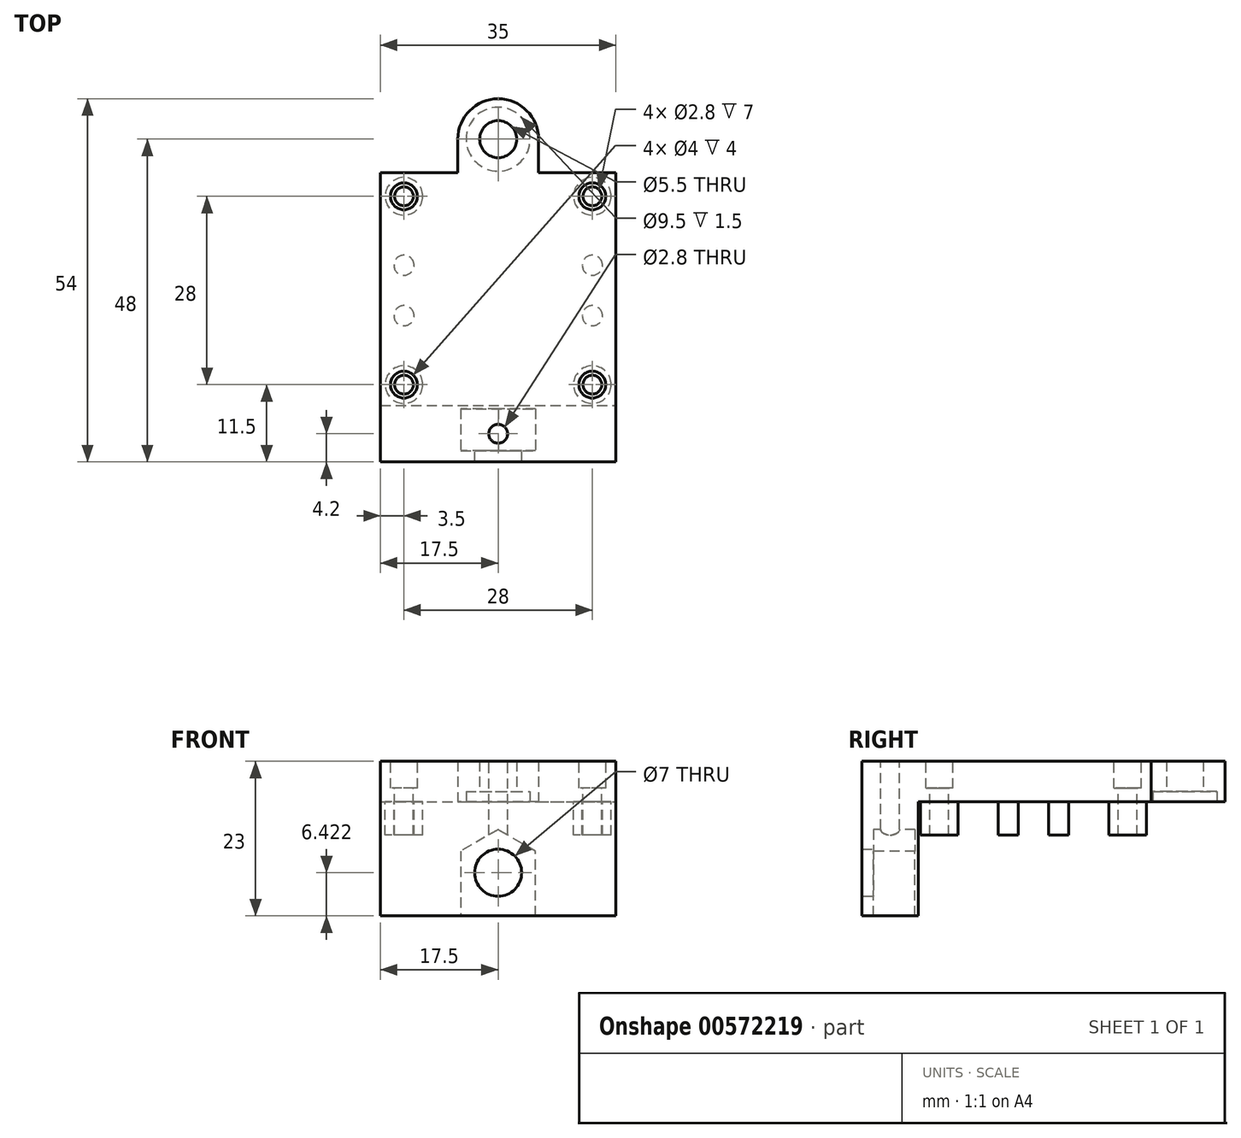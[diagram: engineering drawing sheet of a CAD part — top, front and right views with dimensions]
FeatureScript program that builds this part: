
annotation { "Feature Type Name" : "Feature", "Feature Type Description" : "" }
export const myFeature = defineFeature(function(context is Context, id is Id, definition is map)
    precondition{}
    {
        {
            var Q0;
            Q0=qCreatedBy(makeId("Top.planeOp"),FACE);
            var sketch = newSketch(context, id + "F0", { "sketchPlane" : qUnion([Q0])});
            skLineSegment(sketch, "E0.bottom", {"start": v(-14, 14) * mm, "end": v(14, 14) * mm, "construction": true});
            skLineSegment(sketch, "E0.top", {"start": v(-14, -14) * mm, "end": v(14, -14) * mm, "construction": true});
            skLineSegment(sketch, "E0.left", {"start": v(-14, 14) * mm, "end": v(-14, -14) * mm, "construction": true});
            skLineSegment(sketch, "E0.right", {"start": v(14, 14) * mm, "end": v(14, -14) * mm, "construction": true});
            skPoint(sketch, "E0.middle", {"position": v(0, 0) * mm});
            skLineSegment(sketch, "E1.bottom", {"start": v(-17.5, 17.5) * mm, "end": v(17.5, 17.5) * mm});
            skLineSegment(sketch, "E1.top", {"start": v(-17.5, -17.5) * mm, "end": v(17.5, -17.5) * mm});
            skLineSegment(sketch, "E1.left", {"start": v(-17.5, 17.5) * mm, "end": v(-17.5, -17.5) * mm});
            skLineSegment(sketch, "E1.right", {"start": v(17.5, 17.5) * mm, "end": v(17.5, -17.5) * mm});
            skLineSegment(sketch, "E2.bottom", {"start": v(-6, 22.5) * mm, "end": v(6, 22.5) * mm});
            skPoint(sketch, "E2.middle", {"position": v(0, 17.5) * mm});
            skCircle(sketch, "E3", {"center": v(0, 22.5) * mm, "radius": 6 * mm});
            skLineSegment(sketch, "E4.top", {"start": v(-6, 17.5) * mm, "end": v(6, 17.5) * mm});
            skLineSegment(sketch, "E4.left", {"start": v(-6, 22.5) * mm, "end": v(-6, 17.5) * mm});
            skLineSegment(sketch, "E4.right", {"start": v(6, 22.5) * mm, "end": v(6, 17.5) * mm});
            skCircle(sketch, "E5", {"center": v(-14, 14) * mm, "radius": 2.8 * mm});
            skCircle(sketch, "E6", {"center": v(-14, -14) * mm, "radius": 2.8 * mm});
            skCircle(sketch, "E7", {"center": v(14, -14) * mm, "radius": 2.8 * mm});
            skCircle(sketch, "E8", {"center": v(14, 14) * mm, "radius": 2.8 * mm});
            skCircle(sketch, "E9", {"center": v(-14, 3.75) * mm, "radius": 1.5 * mm});
            skCircle(sketch, "E10", {"center": v(-14, -3.75) * mm, "radius": 1.5 * mm});
            skLineSegment(sketch, "E11", {"start": v(-14, 2.25) * mm, "end": v(-14, -2.25) * mm, "construction": true});
            skPoint(sketch, "E12", {"position": v(-14, 0) * mm});
            skPoint(sketch, "E13", {"position": v(-14, 2.25) * mm});
            skPoint(sketch, "E14", {"position": v(-14, -2.25) * mm});
            skCircle(sketch, "E15", {"center": v(14, -3.75) * mm, "radius": 1.5 * mm});
            skCircle(sketch, "E16", {"center": v(14, 3.75) * mm, "radius": 1.5 * mm});
            skSolve(sketch);
        }
        {
            var Q0;
            Q0=makeQuery(id+"F0.imprint","IMPRINT",FACE,{"disambiguationData":[TD([[makeQuery(id+"F0.imprint","IMPRINT",EDGE,{"derivedFrom":sQuery(id+"F0.wireOp",EDGE,"E1.top")}),1.0]])]});
            var Q1;
            {var subQ0=sQuery(id+"F0.wireOp",EDGE,"E2.bottom");Q1=makeQuery(id+"F0.imprint","IMPRINT",FACE,{"disambiguationData":[TD([[makeQuery(id+"F0.imprint","IMPRINT",EDGE,{"derivedFrom":subQ0}),-1.0]])]});}
            var Q2;
            {var subQ0=sQuery(id+"F0.wireOp",EDGE,"E2.bottom");Q2=makeQuery(id+"F0.imprint","IMPRINT",FACE,{"disambiguationData":[TD([[makeQuery(id+"F0.imprint","IMPRINT",EDGE,{"derivedFrom":subQ0}),1.0]])]});}
            var Q3;
            {var subQ0=sQuery(id+"F0.wireOp",EDGE,"E4.right");Q3=makeQuery(id+"F0.imprint","IMPRINT",FACE,{"disambiguationData":[TD([[makeQuery(id+"F0.imprint","IMPRINT",EDGE,{"derivedFrom":subQ0}),-1.0]])]});}
            var Q4;
            {var subQ0=sQuery(id+"F0.wireOp",EDGE,"E4.top");var subQ1=sQuery(id+"F0.wireOp",EDGE,"E3");var subQ2=makeQuery(id+"F0.imprint","INTERSECT",VERTEX,{"disambiguationData":[OD(0.0)],"derivedFrom":[subQ1,subQ0]});Q4=makeQuery(id+"F0.imprint","IMPRINT",FACE,{"disambiguationData":[TD([[makeQuery(id+"F0.imprint","IMPRINT",EDGE,{"disambiguationData":[TD([[subQ2,-1.0]])],"derivedFrom":subQ1}),1.0]])]});}
            var Q5;
            {var subQ0=sQuery(id+"F0.wireOp",EDGE,"E4.left");Q5=makeQuery(id+"F0.imprint","IMPRINT",FACE,{"disambiguationData":[TD([[makeQuery(id+"F0.imprint","IMPRINT",EDGE,{"derivedFrom":subQ0}),1.0]])]});}
            var Q6;
            Q6=makeQuery(id+"F0.imprint","IMPRINT",FACE,{"disambiguationData":[TD([[makeQuery(id+"F0.imprint","IMPRINT",EDGE,{"derivedFrom":sQuery(id+"F0.wireOp",EDGE,"E6")}),1.0]])]});
            var Q7;
            Q7=makeQuery(id+"F0.imprint","IMPRINT",FACE,{"disambiguationData":[TD([[makeQuery(id+"F0.imprint","IMPRINT",EDGE,{"derivedFrom":sQuery(id+"F0.wireOp",EDGE,"E7")}),1.0]])]});
            var Q8;
            Q8=makeQuery(id+"F0.imprint","IMPRINT",FACE,{"disambiguationData":[TD([[makeQuery(id+"F0.imprint","IMPRINT",EDGE,{"derivedFrom":sQuery(id+"F0.wireOp",EDGE,"E8")}),1.0]])]});
            var Q9;
            Q9=makeQuery(id+"F0.imprint","IMPRINT",FACE,{"disambiguationData":[TD([[makeQuery(id+"F0.imprint","IMPRINT",EDGE,{"derivedFrom":sQuery(id+"F0.wireOp",EDGE,"E5")}),1.0]])]});
            var Q10;
            Q10=makeQuery(id+"F0.imprint","IMPRINT",FACE,{"disambiguationData":[TD([[makeQuery(id+"F0.imprint","IMPRINT",EDGE,{"derivedFrom":sQuery(id+"F0.wireOp",EDGE,"E9")}),1.0]])]});
            var Q11;
            Q11=makeQuery(id+"F0.imprint","IMPRINT",FACE,{"disambiguationData":[TD([[makeQuery(id+"F0.imprint","IMPRINT",EDGE,{"derivedFrom":sQuery(id+"F0.wireOp",EDGE,"E10")}),1.0]])]});
            var Q12;
            Q12=makeQuery(id+"F0.imprint","IMPRINT",FACE,{"disambiguationData":[TD([[makeQuery(id+"F0.imprint","IMPRINT",EDGE,{"derivedFrom":sQuery(id+"F0.wireOp",EDGE,"E15")}),1.0]])]});
            var Q13;
            Q13=makeQuery(id+"F0.imprint","IMPRINT",FACE,{"disambiguationData":[TD([[makeQuery(id+"F0.imprint","IMPRINT",EDGE,{"derivedFrom":sQuery(id+"F0.wireOp",EDGE,"E16")}),1.0]])]});
            extrude(context, id + "F1", {"entities" : qUnion([Q0, Q1, Q2, Q3, Q4, Q5, Q6, Q7, Q8, Q9, Q10, Q11, Q12, Q13]), "depth" : 6 * mm, "offsetDistance" : 25 * mm});
        }
        {
            var Q0;
            Q0=makeQuery(id+"F0.imprint","IMPRINT",FACE,{"disambiguationData":[TD([[makeQuery(id+"F0.imprint","IMPRINT",EDGE,{"derivedFrom":sQuery(id+"F0.wireOp",EDGE,"E6")}),1.0]])]});
            var Q1;
            Q1=makeQuery(id+"F0.imprint","IMPRINT",FACE,{"disambiguationData":[TD([[makeQuery(id+"F0.imprint","IMPRINT",EDGE,{"derivedFrom":sQuery(id+"F0.wireOp",EDGE,"E5")}),1.0]])]});
            var Q2;
            Q2=makeQuery(id+"F0.imprint","IMPRINT",FACE,{"disambiguationData":[TD([[makeQuery(id+"F0.imprint","IMPRINT",EDGE,{"derivedFrom":sQuery(id+"F0.wireOp",EDGE,"E8")}),1.0]])]});
            var Q3;
            Q3=makeQuery(id+"F0.imprint","IMPRINT",FACE,{"disambiguationData":[TD([[makeQuery(id+"F0.imprint","IMPRINT",EDGE,{"derivedFrom":sQuery(id+"F0.wireOp",EDGE,"E7")}),1.0]])]});
            var Q4;
            Q4=makeQuery(id+"F0.imprint","IMPRINT",FACE,{"disambiguationData":[TD([[makeQuery(id+"F0.imprint","IMPRINT",EDGE,{"derivedFrom":sQuery(id+"F0.wireOp",EDGE,"E9")}),1.0]])]});
            var Q5;
            Q5=makeQuery(id+"F0.imprint","IMPRINT",FACE,{"disambiguationData":[TD([[makeQuery(id+"F0.imprint","IMPRINT",EDGE,{"derivedFrom":sQuery(id+"F0.wireOp",EDGE,"E10")}),1.0]])]});
            var Q6;
            Q6=makeQuery(id+"F0.imprint","IMPRINT",FACE,{"disambiguationData":[TD([[makeQuery(id+"F0.imprint","IMPRINT",EDGE,{"derivedFrom":sQuery(id+"F0.wireOp",EDGE,"E15")}),1.0]])]});
            var Q7;
            Q7=makeQuery(id+"F0.imprint","IMPRINT",FACE,{"disambiguationData":[TD([[makeQuery(id+"F0.imprint","IMPRINT",EDGE,{"derivedFrom":sQuery(id+"F0.wireOp",EDGE,"E16")}),1.0]])]});
            extrude(context, id + "F2", {"entities" : qUnion([Q0, Q1, Q2, Q3, Q4, Q5, Q6, Q7]), "operationType" : NewBodyOperationType.ADD, "oppositeDirection" : true, "depth" : 5 * mm, "offsetDistance" : 25 * mm});
        }
        {
            var Q0;
            Q0=sQuery(id+"F0.wireOp",VERTEX,"E3.center");
            var Q1;
            Q1=makeQuery(id+"F1.opExtrude","SWEPT_BODY",BODY,{"disambiguationData":[OSD([sQuery(id+"F0.wireOp",EDGE,"E1.bottom"),sQuery(id+"F0.wireOp",EDGE,"E1.top"),sQuery(id+"F0.wireOp",EDGE,"E1.left"),sQuery(id+"F0.wireOp",EDGE,"E1.right"),sQuery(id+"F0.wireOp",EDGE,"E3"),sQuery(id+"F0.wireOp",EDGE,"E4.left"),sQuery(id+"F0.wireOp",EDGE,"E4.right")])]});
            hole(context, id + "F3", {"style" : HoleStyle.C_BORE, "endStyle" : HoleEndStyle.BLIND, "oppositeDirection" : true, "holeDiameter" : 5.5 * mm, "cBoreDiameter" : 9.5 * mm, "cBoreDepth" : 1.5 * mm, "majorDiameter" : 5 * mm, "holeDepth" : 30 * mm, "isTappedThrough" : true, "tappedDepth" : 10.5 * mm, "tapClearance" : 3, "locations" : qUnion([Q0]), "scope" : qUnion([Q1])});
        }
        {
            var Q0;
            Q0=makeQuery(id+"F1.opExtrude","CAP_FACE",FACE,{"disambiguationData":[OSD([sQuery(id+"F0.wireOp",EDGE,"E1.bottom"),sQuery(id+"F0.wireOp",EDGE,"E1.top"),sQuery(id+"F0.wireOp",EDGE,"E1.left"),sQuery(id+"F0.wireOp",EDGE,"E1.right"),sQuery(id+"F0.wireOp",EDGE,"E3"),sQuery(id+"F0.wireOp",EDGE,"E4.left"),sQuery(id+"F0.wireOp",EDGE,"E4.right")])],"isStart":false});
            var sketch = newSketch(context, id + "F4", { "sketchPlane" : qUnion([Q0])});
            skPoint(sketch, "E17", {"position": v(-14, 14) * mm});
            skPoint(sketch, "E18", {"position": v(14, 14) * mm});
            skPoint(sketch, "E19", {"position": v(-14, -14) * mm});
            skPoint(sketch, "E20", {"position": v(14, -14) * mm});
            skSolve(sketch);
        }
        {
            var Q0;
            Q0=sQuery(id+"F4.wireOp",VERTEX,"E17");
            var Q1;
            Q1=sQuery(id+"F4.wireOp",VERTEX,"E18");
            var Q2;
            Q2=sQuery(id+"F4.wireOp",VERTEX,"E20");
            var Q3;
            Q3=sQuery(id+"F4.wireOp",VERTEX,"E19");
            var Q4;
            Q4=makeQuery(id+"F1.opExtrude","SWEPT_BODY",BODY,{"disambiguationData":[OSD([sQuery(id+"F0.wireOp",EDGE,"E1.bottom"),sQuery(id+"F0.wireOp",EDGE,"E1.top"),sQuery(id+"F0.wireOp",EDGE,"E1.left"),sQuery(id+"F0.wireOp",EDGE,"E1.right"),sQuery(id+"F0.wireOp",EDGE,"E3"),sQuery(id+"F0.wireOp",EDGE,"E4.left"),sQuery(id+"F0.wireOp",EDGE,"E4.right")])]});
            hole(context, id + "F5", {"style" : HoleStyle.C_BORE, "endStyle" : HoleEndStyle.THROUGH, "holeDiameter" : 2.8 * mm, "cBoreDiameter" : 4 * mm, "cBoreDepth" : 4 * mm, "majorDiameter" : 5 * mm, "isTappedThrough" : true, "tappedDepth" : 10.5 * mm, "tapClearance" : 3, "locations" : qUnion([Q0, Q1, Q2, Q3]), "scope" : qUnion([Q4])});
        }
        {
            var Q0;
            Q0=makeQuery(id+"F1.opExtrude","SWEPT_FACE",FACE,{"disambiguationData":[OSD([sQuery(id+"F0.wireOp",EDGE,"E1.top")])]});
            var sketch = newSketch(context, id + "F6", { "sketchPlane" : qUnion([Q0])});
            skLineSegment(sketch, "E21.bottom", {"start": v(-17.5, 6) * mm, "end": v(17.5, 6) * mm});
            skLineSegment(sketch, "E21.top", {"start": v(-17.5, -17) * mm, "end": v(17.5, -17) * mm});
            skLineSegment(sketch, "E21.left", {"start": v(-17.5, 6) * mm, "end": v(-17.5, -17) * mm});
            skLineSegment(sketch, "E21.right", {"start": v(17.5, 6) * mm, "end": v(17.5, -17) * mm});
            skSolve(sketch);
        }
        {
            var Q0;
            {var subQ0=sQuery(id+"F6.wireOp",EDGE,"E21.top");Q0=makeQuery(id+"F6.imprint","IMPRINT",FACE,{"disambiguationData":[TD([[makeQuery(id+"F6.imprint","IMPRINT",EDGE,{"derivedFrom":subQ0}),1.0]])]});}
            var Q1;
            {var subQ0=sQuery(id+"F6.wireOp",EDGE,"E21.bottom");Q1=makeQuery(id+"F6.imprint","IMPRINT",FACE,{"disambiguationData":[TD([[makeQuery(id+"F6.imprint","IMPRINT",EDGE,{"derivedFrom":subQ0}),-1.0]])]});}
            extrude(context, id + "F7", {"entities" : qUnion([Q0, Q1]), "operationType" : NewBodyOperationType.ADD, "depth" : 8 * mm, "offsetDistance" : 25 * mm, "hasSecondDirection" : true, "secondDirectionOppositeDirection" : true, "secondDirectionDepth" : 0.4 * mm});
        }
        {
            var Q0;
            Q0=makeQuery(id+"F7.opExtrude","CAP_FACE",FACE,{"disambiguationData":[OSD([sQuery(id+"F6.wireOp",EDGE,"E21.bottom"),sQuery(id+"F6.wireOp",EDGE,"E21.top"),sQuery(id+"F6.wireOp",EDGE,"E21.left"),sQuery(id+"F6.wireOp",EDGE,"E21.right")])],"isStart":true});
            var Q1;
            Q1=makeQuery(id+"F7.opExtrude","CAP_FACE",FACE,{"disambiguationData":[OSD([sQuery(id+"F6.wireOp",EDGE,"E21.bottom"),sQuery(id+"F6.wireOp",EDGE,"E21.top"),sQuery(id+"F6.wireOp",EDGE,"E21.left"),sQuery(id+"F6.wireOp",EDGE,"E21.right")])],"isStart":false});
            cPlane(context, id + "F8", {"entities" : qUnion([Q0, Q1]), "cplaneType" : CPlaneType.MID_PLANE, "offset" : 25 * mm, "width" : 150 * mm, "height" : 150 * mm});
        }
        {
            var Q0;
            Q0=qCreatedBy(id+"F8.planeOp",FACE);
            var sketch = newSketch(context, id + "F9", { "sketchPlane" : qUnion([Q0])});
            skCircle(sketch, "E22.cCircle", {"center": v(0, -10.58) * mm, "radius": 5.56 * mm, "construction": true});
            skLineSegment(sketch, "E22.0", {"start": v(-5.56, -13.79) * mm, "end": v(-5.56, -7.37) * mm});
            skLineSegment(sketch, "E22.1", {"start": v(-5.56, -7.37) * mm, "end": v(0, -4.16) * mm});
            skLineSegment(sketch, "E22.2", {"start": v(0, -4.16) * mm, "end": v(5.56, -7.37) * mm});
            skLineSegment(sketch, "E22.3", {"start": v(5.56, -7.37) * mm, "end": v(5.56, -13.79) * mm});
            skLineSegment(sketch, "E22.4", {"start": v(5.56, -13.79) * mm, "end": v(0, -17) * mm});
            skLineSegment(sketch, "E22.5", {"start": v(0, -17) * mm, "end": v(-5.56, -13.79) * mm});
            skPoint(sketch, "E22.0.midPoint", {"position": v(-5.56, -10.58) * mm});
            skLineSegment(sketch, "E23.bottom", {"start": v(5.56, -13.79) * mm, "end": v(-5.56, -13.79) * mm});
            skLineSegment(sketch, "E23.top", {"start": v(5.56, -17) * mm, "end": v(-5.56, -17) * mm});
            skLineSegment(sketch, "E23.left", {"start": v(5.56, -13.79) * mm, "end": v(5.56, -17) * mm});
            skLineSegment(sketch, "E23.right", {"start": v(-5.56, -13.79) * mm, "end": v(-5.56, -17) * mm});
            skSolve(sketch);
        }
        {
            var Q0;
            Q0 = qSketchRegion(id + "F9", true);
            extrude(context, id + "F10", {"entities" : qUnion([Q0]), "operationType" : NewBodyOperationType.REMOVE, "depth" : 3.7 * mm, "offsetDistance" : 25 * mm, "hasSecondDirection" : true, "secondDirectionOppositeDirection" : true, "secondDirectionDepth" : 2.5 * mm});
        }
        {
            var Q0;
            Q0=sQuery(id+"F9.wireOp",VERTEX,"E22.cCircle.center");
            var Q1;
            Q1=makeQuery(id+"F1.opExtrude","SWEPT_BODY",BODY,{"disambiguationData":[OSD([sQuery(id+"F0.wireOp",EDGE,"E1.bottom"),sQuery(id+"F0.wireOp",EDGE,"E1.top"),sQuery(id+"F0.wireOp",EDGE,"E1.left"),sQuery(id+"F0.wireOp",EDGE,"E1.right"),sQuery(id+"F0.wireOp",EDGE,"E3"),sQuery(id+"F0.wireOp",EDGE,"E4.left"),sQuery(id+"F0.wireOp",EDGE,"E4.right")])]});
            hole(context, id + "F11", {"style" : HoleStyle.SIMPLE, "endStyle" : HoleEndStyle.THROUGH, "holeDiameter" : 7 * mm, "majorDiameter" : 5 * mm, "isTappedThrough" : true, "tappedDepth" : 10.5 * mm, "tapClearance" : 3, "locations" : qUnion([Q0]), "scope" : qUnion([Q1])});
        }
        {
            var Q0;
            Q0=makeQuery(id+"F7.boolean.opBoolean","MERGE",FACE,{"derivedFrom":[makeQuery(id+"F1.opExtrude","CAP_FACE",FACE,{"disambiguationData":[OSD([sQuery(id+"F0.wireOp",EDGE,"E1.bottom"),sQuery(id+"F0.wireOp",EDGE,"E1.top"),sQuery(id+"F0.wireOp",EDGE,"E1.left"),sQuery(id+"F0.wireOp",EDGE,"E1.right"),sQuery(id+"F0.wireOp",EDGE,"E3"),sQuery(id+"F0.wireOp",EDGE,"E4.left"),sQuery(id+"F0.wireOp",EDGE,"E4.right")])],"isStart":false}),makeQuery(id+"F7.opExtrude","SWEPT_FACE",FACE,{"disambiguationData":[OSD([sQuery(id+"F6.wireOp",EDGE,"E21.bottom")])]})]});
            var sketch = newSketch(context, id + "F12", { "sketchPlane" : qUnion([Q0])});
            skPoint(sketch, "E24", {"position": v(0, -21.3) * mm});
            skSolve(sketch);
        }
        {
            var Q0;
            Q0=sQuery(id+"F12.wireOp",VERTEX,"E24");
            var Q1;
            Q1=makeQuery(id+"F1.opExtrude","SWEPT_BODY",BODY,{"disambiguationData":[OSD([sQuery(id+"F0.wireOp",EDGE,"E1.bottom"),sQuery(id+"F0.wireOp",EDGE,"E1.top"),sQuery(id+"F0.wireOp",EDGE,"E1.left"),sQuery(id+"F0.wireOp",EDGE,"E1.right"),sQuery(id+"F0.wireOp",EDGE,"E3"),sQuery(id+"F0.wireOp",EDGE,"E4.left"),sQuery(id+"F0.wireOp",EDGE,"E4.right")])]});
            hole(context, id + "F13", {"style" : HoleStyle.SIMPLE, "endStyle" : HoleEndStyle.THROUGH, "holeDiameter" : 2.8 * mm, "majorDiameter" : 5 * mm, "isTappedThrough" : true, "tappedDepth" : 10.5 * mm, "tapClearance" : 3, "locations" : qUnion([Q0]), "scope" : qUnion([Q1])});
        }
    });
